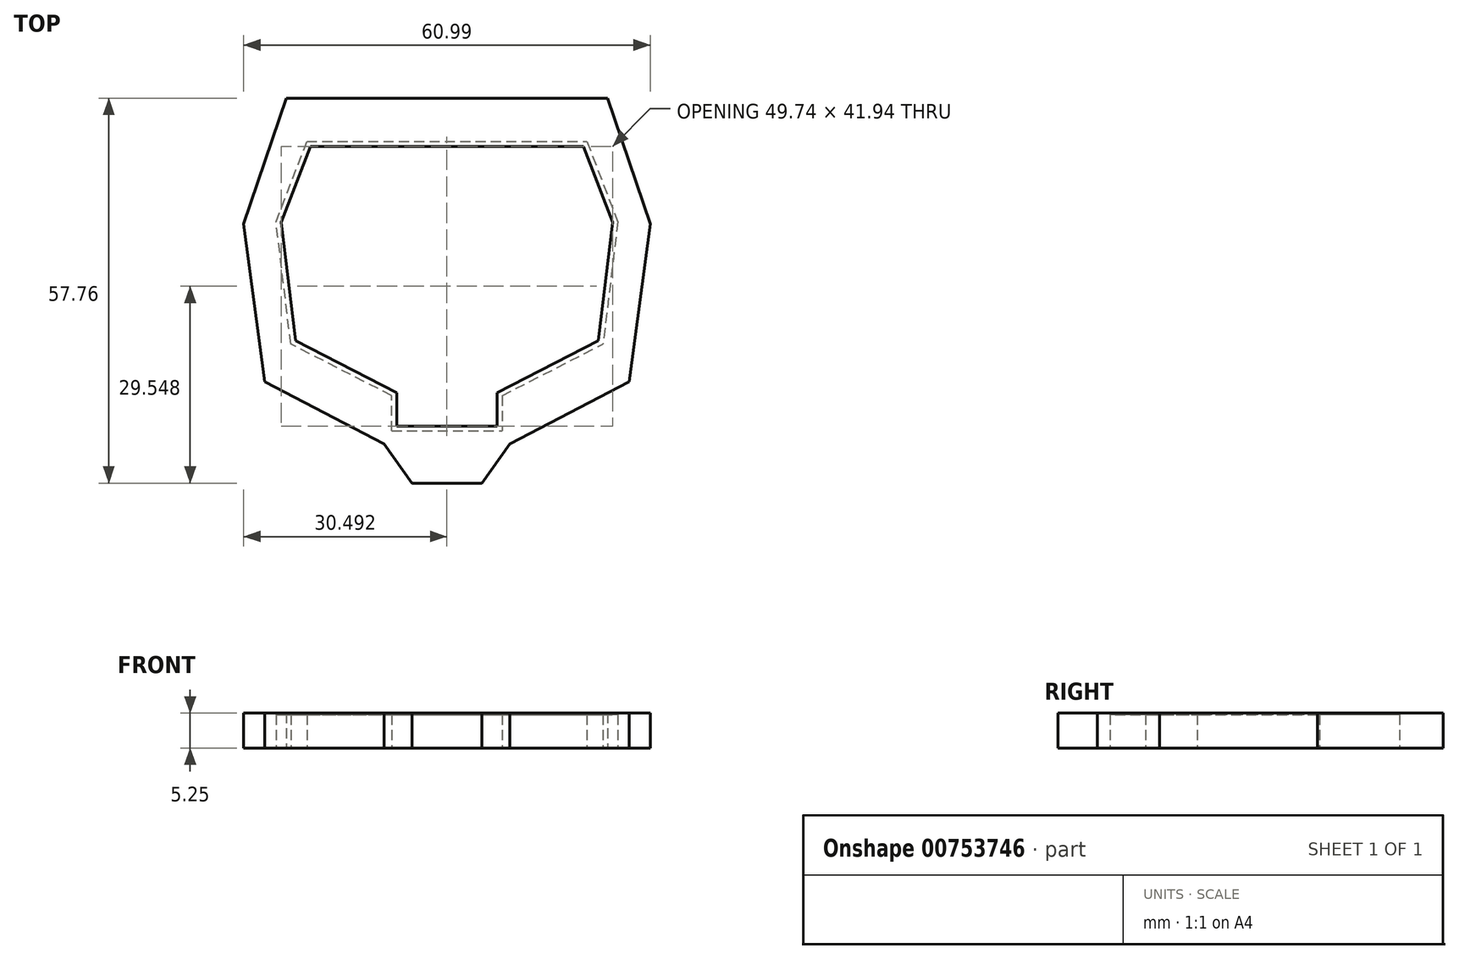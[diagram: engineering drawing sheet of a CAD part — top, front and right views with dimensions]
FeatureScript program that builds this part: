
annotation { "Feature Type Name" : "Feature", "Feature Type Description" : "" }
export const myFeature = defineFeature(function(context is Context, id is Id, definition is map)
    precondition{}
    {
        {
            var Q0;
            Q0=qCreatedBy(makeId("Top.planeOp"),FACE);
            var sketch = newSketch(context, id + "F0", { "sketchPlane" : qUnion([Q0])});
            skLineSegment(sketch, "E0.0", {"start": v(24.01, 32.97) * mm, "end": v(-24.13, 32.97) * mm});
            skLineSegment(sketch, "E1.0", {"start": v(-30.55, 14.15) * mm, "end": v(-24.13, 32.97) * mm});
            skLineSegment(sketch, "E2.0", {"start": v(-21.06, 26.48) * mm, "end": v(20.94, 26.48) * mm});
            skLineSegment(sketch, "E3.0", {"start": v(-25.7, 14.45) * mm, "end": v(-21.06, 26.48) * mm});
            skLineSegment(sketch, "E4.0", {"start": v(-27.4, -9.55) * mm, "end": v(-30.55, 14.15) * mm});
            skLineSegment(sketch, "E5.0", {"start": v(-23.47, -3.92) * mm, "end": v(-25.7, 14.45) * mm});
            skLineSegment(sketch, "E6.0", {"start": v(-8.34, -11.66) * mm, "end": v(-23.47, -3.92) * mm});
            skLineSegment(sketch, "E7.0", {"start": v(-9.5, -18.88) * mm, "end": v(-27.4, -9.55) * mm});
            skLineSegment(sketch, "E8.0", {"start": v(-8.34, -16.96) * mm, "end": v(-8.34, -11.66) * mm});
            skLineSegment(sketch, "E9.0", {"start": v(-8.34, -16.96) * mm, "end": v(8.22, -16.96) * mm});
            skLineSegment(sketch, "E10.0", {"start": v(-5.29, -24.8) * mm, "end": v(-9.5, -18.88) * mm});
            skLineSegment(sketch, "E11.0", {"start": v(5.17, -24.8) * mm, "end": v(-5.29, -24.8) * mm});
            skPoint(sketch, "E12.0", {"position": v(9.4, -18.88) * mm});
            skLineSegment(sketch, "E13.0", {"start": v(9.4, -18.88) * mm, "end": v(5.17, -24.8) * mm});
            skLineSegment(sketch, "E14.0", {"start": v(27.28, -9.55) * mm, "end": v(9.4, -18.88) * mm});
            skLineSegment(sketch, "E15.0", {"start": v(8.22, -11.66) * mm, "end": v(23.36, -3.92) * mm});
            skLineSegment(sketch, "E16.0", {"start": v(30.44, 14.15) * mm, "end": v(27.28, -9.55) * mm});
            skLineSegment(sketch, "E17.0", {"start": v(30.44, 14.15) * mm, "end": v(24.01, 32.97) * mm});
            skLineSegment(sketch, "E18.0", {"start": v(20.94, 26.48) * mm, "end": v(25.58, 14.45) * mm});
            skLineSegment(sketch, "E19.0", {"start": v(25.58, 14.45) * mm, "end": v(23.36, -3.92) * mm});
            skLineSegment(sketch, "E20", {"start": v(8.22, -11.66) * mm, "end": v(8.22, -16.96) * mm});
            skSolve(sketch);
        }
        {
            var Q0;
            Q0 = qSketchRegion(id + "F0", true);
            extrude(context, id + "F1", {"entities" : qUnion([Q0]), "depth" : 5 * mm, "offsetDistance" : 25.4 * mm});
        }
        {
            var Q0;
            Q0=makeQuery(id+"F1.opExtrude","CAP_FACE",FACE,{"disambiguationData":[OSD([sQuery(id+"F0.wireOp",EDGE,"E0.0"),sQuery(id+"F0.wireOp",EDGE,"E1.0"),sQuery(id+"F0.wireOp",EDGE,"E2.0"),sQuery(id+"F0.wireOp",EDGE,"E3.0"),sQuery(id+"F0.wireOp",EDGE,"E4.0"),sQuery(id+"F0.wireOp",EDGE,"E5.0"),sQuery(id+"F0.wireOp",EDGE,"E6.0"),sQuery(id+"F0.wireOp",EDGE,"E7.0"),sQuery(id+"F0.wireOp",EDGE,"E8.0"),sQuery(id+"F0.wireOp",EDGE,"E9.0"),sQuery(id+"F0.wireOp",EDGE,"E10.0"),sQuery(id+"F0.wireOp",EDGE,"E11.0"),sQuery(id+"F0.wireOp",EDGE,"E13.0"),sQuery(id+"F0.wireOp",EDGE,"E14.0"),sQuery(id+"F0.wireOp",EDGE,"E15.0"),sQuery(id+"F0.wireOp",EDGE,"E16.0"),sQuery(id+"F0.wireOp",EDGE,"E17.0"),sQuery(id+"F0.wireOp",EDGE,"E18.0"),sQuery(id+"F0.wireOp",EDGE,"E19.0"),sQuery(id+"F0.wireOp",EDGE,"E20")])],"isStart":false});
            var sketch = newSketch(context, id + "F2", { "sketchPlane" : qUnion([Q0])});
            skLineSegment(sketch, "E21.0", {"start": v(-21.06, 26.48) * mm, "end": v(20.94, 26.48) * mm});
            skPoint(sketch, "E22.0", {"position": v(-23.38, 20.46) * mm});
            skLineSegment(sketch, "E23.0", {"start": v(-25.7, 14.45) * mm, "end": v(-21.06, 26.48) * mm});
            skPoint(sketch, "E24.0", {"position": v(-24.59, 5.27) * mm});
            skLineSegment(sketch, "E25.0", {"start": v(-23.47, -3.92) * mm, "end": v(-25.7, 14.45) * mm});
            skLineSegment(sketch, "E26.0", {"start": v(-8.34, -11.66) * mm, "end": v(-23.47, -3.92) * mm});
            skLineSegment(sketch, "E27.0", {"start": v(-8.34, -16.96) * mm, "end": v(-8.34, -11.66) * mm});
            skLineSegment(sketch, "E28.0", {"start": v(-8.34, -16.96) * mm, "end": v(8.22, -16.96) * mm});
            skLineSegment(sketch, "E29.0", {"start": v(8.22, -11.66) * mm, "end": v(8.22, -16.96) * mm});
            skLineSegment(sketch, "E30.0", {"start": v(8.22, -11.66) * mm, "end": v(23.36, -3.92) * mm});
            skLineSegment(sketch, "E31.0", {"start": v(25.58, 14.45) * mm, "end": v(23.36, -3.92) * mm});
            skLineSegment(sketch, "E32.0", {"start": v(20.94, 26.48) * mm, "end": v(25.58, 14.45) * mm});
            skLineSegment(sketch, "E33.0", {"start": v(24.01, 32.97) * mm, "end": v(-24.13, 32.97) * mm});
            skLineSegment(sketch, "E34.0", {"start": v(30.44, 14.15) * mm, "end": v(24.01, 32.97) * mm});
            skLineSegment(sketch, "E35.0", {"start": v(30.44, 14.15) * mm, "end": v(27.28, -9.55) * mm});
            skLineSegment(sketch, "E36.0", {"start": v(27.28, -9.55) * mm, "end": v(9.4, -18.88) * mm});
            skLineSegment(sketch, "E37.0", {"start": v(9.4, -18.88) * mm, "end": v(5.17, -24.8) * mm});
            skLineSegment(sketch, "E38.0", {"start": v(5.17, -24.8) * mm, "end": v(-5.29, -24.8) * mm});
            skLineSegment(sketch, "E39.0", {"start": v(-5.29, -24.8) * mm, "end": v(-9.5, -18.88) * mm});
            skLineSegment(sketch, "E40.0", {"start": v(-9.5, -18.88) * mm, "end": v(-27.4, -9.55) * mm});
            skLineSegment(sketch, "E41.0", {"start": v(-27.4, -9.55) * mm, "end": v(-30.55, 14.15) * mm});
            skLineSegment(sketch, "E42.0", {"start": v(-30.55, 14.15) * mm, "end": v(-24.13, 32.97) * mm});
            skLineSegment(sketch, "E43.0", {"start": v(-24.93, 14.35) * mm, "end": v(-20.54, 25.73) * mm});
            skLineSegment(sketch, "E43.1", {"start": v(-22.78, -3.43) * mm, "end": v(-24.93, 14.35) * mm});
            skLineSegment(sketch, "E43.2", {"start": v(-20.54, 25.73) * mm, "end": v(20.42, 25.73) * mm});
            skLineSegment(sketch, "E43.3", {"start": v(-7.6, -11.2) * mm, "end": v(-22.78, -3.43) * mm});
            skLineSegment(sketch, "E43.4", {"start": v(-7.6, -16.21) * mm, "end": v(-7.6, -11.2) * mm});
            skLineSegment(sketch, "E43.5", {"start": v(-7.6, -16.21) * mm, "end": v(7.47, -16.21) * mm});
            skLineSegment(sketch, "E43.6", {"start": v(20.42, 25.73) * mm, "end": v(24.81, 14.35) * mm});
            skLineSegment(sketch, "E43.7", {"start": v(24.81, 14.35) * mm, "end": v(22.66, -3.43) * mm});
            skLineSegment(sketch, "E43.8", {"start": v(7.47, -11.2) * mm, "end": v(22.66, -3.43) * mm});
            skLineSegment(sketch, "E43.9", {"start": v(7.47, -11.2) * mm, "end": v(7.47, -16.21) * mm});
            skSolve(sketch);
        }
        {
            var Q0;
            Q0 = qSketchRegion(id + "F2", true);
            var Q1;
            Q1=makeQuery(id+"F2.imprint","IMPRINT",FACE,{"disambiguationData":[TD([[makeQuery(id+"F2.imprint","IMPRINT",EDGE,{"derivedFrom":sQuery(id+"F2.wireOp",EDGE,"E21.0")}),-1.0]])]});
            extrude(context, id + "F3", {"entities" : qUnion([Q0, Q1]), "operationType" : NewBodyOperationType.ADD, "depth" : 0.25 * mm, "offsetDistance" : 25.4 * mm});
        }
    });
